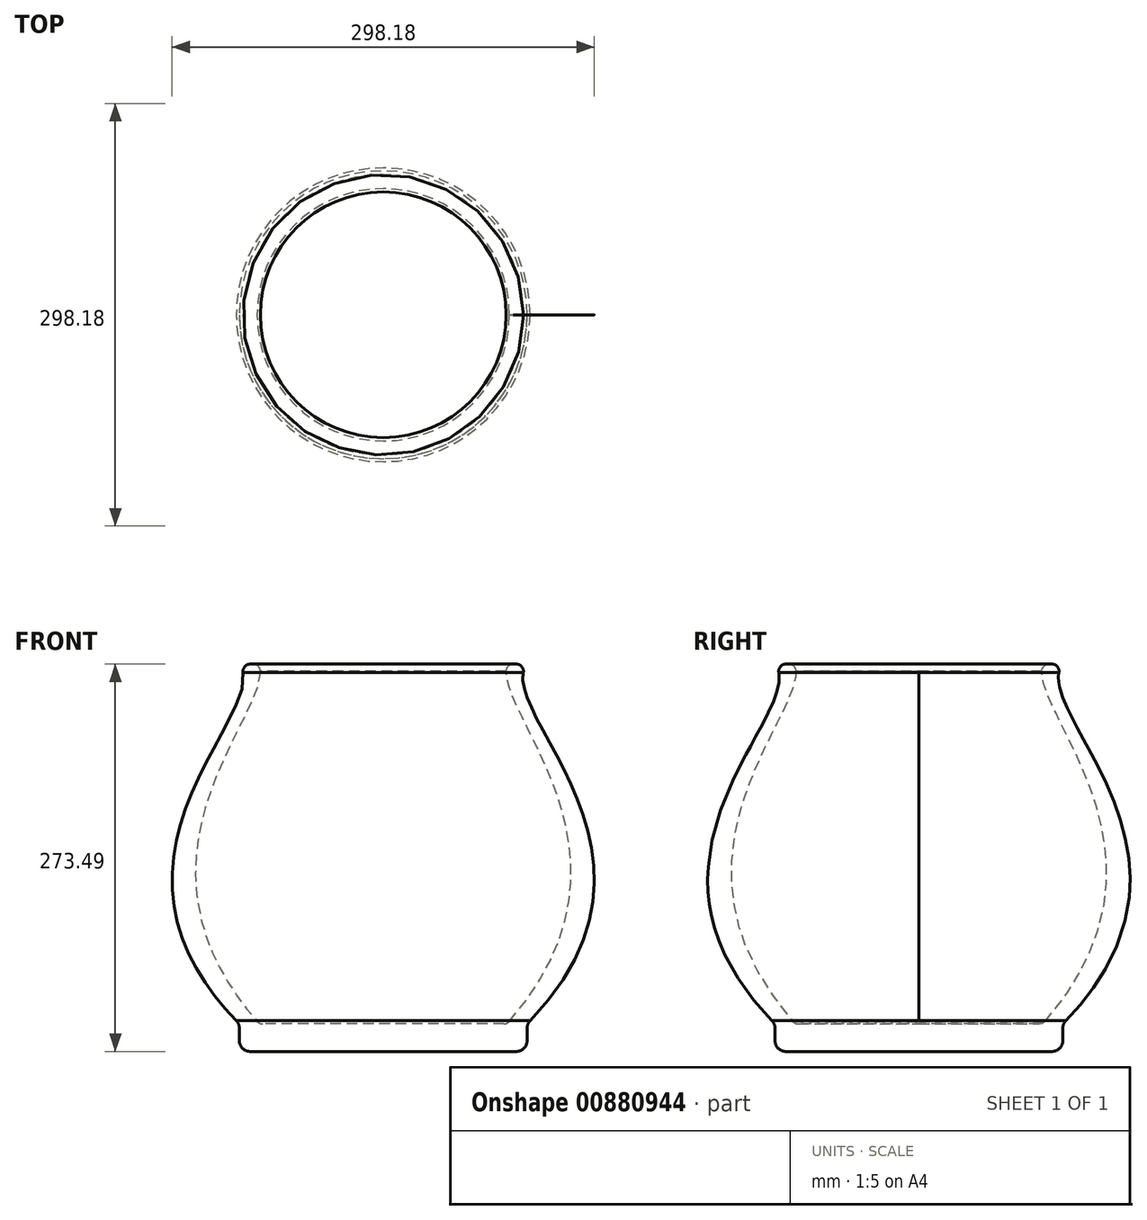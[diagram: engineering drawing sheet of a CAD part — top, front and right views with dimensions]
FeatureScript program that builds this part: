
annotation { "Feature Type Name" : "Feature", "Feature Type Description" : "" }
export const myFeature = defineFeature(function(context is Context, id is Id, definition is map)
    precondition{}
    {
        {
            var Q0;
            Q0=qCreatedBy(makeId("Front.planeOp"),FACE);
            var sketch = newSketch(context, id + "F0", { "sketchPlane" : qUnion([Q0])});
            skLineSegment(sketch, "E0", {"start": v(0, 133.3) * mm, "end": v(0, -120.7) * mm});
            skLineSegment(sketch, "E1", {"start": v(0, -120.7) * mm, "end": v(-87.52, -120.7) * mm});
            skLineSegment(sketch, "E2", {"start": v(0, 133.3) * mm, "end": v(-101.6, 133.3) * mm});
            skLineSegment(sketch, "E3", {"start": v(0, 0) * mm, "end": v(-76.2, 0) * mm});
            skFitSpline(sketch, "E4", {"points": [v(-101.6, -120.7) * mm, v(-101.6, 133.3) * mm], "startDerivative": vector(-355.73, 362.1) * mm, "endDerivative": vector(-76.2, 100.24) * mm});
            skFitSpline(sketch, "E5", {"points": [v(-87.52, -120.7) * mm, v(-87.52, 133.3) * mm], "startDerivative": vector(-320.33, 362.1) * mm, "endDerivative": vector(-33.97, 100.24) * mm});
            skLineSegment(sketch, "E6", {"start": v(-87.52, 133.3) * mm, "end": v(0, 133.3) * mm});
            skLineSegment(sketch, "E7", {"start": v(-87.52, -120.7) * mm, "end": v(0, -120.7) * mm});
            skLineSegment(sketch, "E8", {"start": v(-101.6, 133.3) * mm, "end": v(0, 133.3) * mm});
            skLineSegment(sketch, "E9", {"start": v(-101.6, -120.7) * mm, "end": v(-101.6, -140.19) * mm});
            skLineSegment(sketch, "E10", {"start": v(-101.6, -140.19) * mm, "end": v(0, -140.19) * mm});
            skLineSegment(sketch, "E11", {"start": v(0, -140.19) * mm, "end": v(0, -120.7) * mm});
            skSolve(sketch);
        }
        {
            var Q0;
            {var subQ1=sQuery(id+"F0.wireOp",EDGE,"E4");Q0=makeQuery(id+"F0.imprint","IMPRINT",FACE,{"disambiguationData":[TD([[makeQuery(id+"F0.imprint","IMPRINT",EDGE,{"derivedFrom":subQ1}),-1.0]])]});}
            var Q1;
            Q1=sQuery(id+"F0.wireOp",EDGE,"E0");
            revolve(context, id + "F1", {"surfaceOperationType" : NewSurfaceOperationType.NEW, "entities" : qUnion([Q0]), "axis" : qUnion([Q1]), "revolveType" : RevolveType.FULL});
        }
        {
            var Q0;
            Q0=makeQuery(id+"F1.opRevolve","SWEPT_EDGE",EDGE,{"disambiguationData":[OSD([sQuery(id+"F0.wireOp",EDGE,"E9"),sQuery(id+"F0.wireOp",EDGE,"E10")])]});
            var Q1;
            Q1=makeQuery(id+"F1.opRevolve","SWEPT_EDGE",EDGE,{"disambiguationData":[OSD([sQuery(id+"F0.wireOp",EDGE,"E4"),sQuery(id+"F0.wireOp",EDGE,"E9")])]});
            fillet(context, id + "F2", {"entities" : qUnion([Q0, Q1]), "radius" : 7.62 * mm, "tangentPropagation" : true, "allowEdgeOverflow" : false});
        }
        {
            var Q0;
            Q0=makeQuery(id+"F1.opRevolve","SWEPT_EDGE",EDGE,{"disambiguationData":[OSD([sQuery(id+"F0.wireOp",EDGE,"E4"),sQuery(id+"F0.wireOp",EDGE,"E8")])]});
            var Q1;
            Q1=makeQuery(id+"F1.opRevolve","SWEPT_EDGE",EDGE,{"disambiguationData":[OSD([sQuery(id+"F0.wireOp",EDGE,"E5"),sQuery(id+"F0.wireOp",EDGE,"E8")])]});
            fillet(context, id + "F3", {"entities" : qUnion([Q0, Q1]), "radius" : 5.08 * mm, "tangentPropagation" : true, "allowEdgeOverflow" : false});
        }
    });
